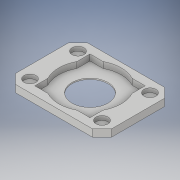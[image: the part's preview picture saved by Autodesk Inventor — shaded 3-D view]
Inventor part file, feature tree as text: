
AUTODESK INVENTOR PART (.ipt)
format: ipt  version: 2019 (Build 230136000, 136)  size: 176,128 bytes
history: native  units: mm
features: extrude x5, sketch x5, chamfer x4
ambient origin geometry x8: Origin, YZ Plane, XZ Plane, XY Plane, X Axis, Y Axis, Z Axis, Center Point
bodies: Solid1 (feature_tree)
feature tree (14):
  extrude  "Extrusion1"  Depth=40.0mm
  extrude  "Extrusion2"  Depth=3.0mm
  extrude  "Extrusion3"  Depth=2.5mm TaperAngle=0.0deg
  extrude  "Extrusion4"  Depth=3.5mm TaperAngle=0.0deg
  chamfer  "Chamfer1"  Distance=5.0mm
  chamfer  "Chamfer2"  Distance=5.0mm
  chamfer  "Chamfer3"  Distance=5.0mm
  chamfer  "Chamfer4"  Distance=15.0mm
  extrude  "Extrusion5"  Depth=2.5mm
  sketch  "Sketch1"  dims[d0=30.0mm d1=40.0mm]
  sketch  "Sketch2"  dims[d2=3.0mm d3=0.0mm d4=20.0mm]
  sketch  "Sketch3"  dims[d5=26.0mm d6=2.5mm d7=0.0mm]
  sketch  "Sketch4"  dims[d8=15.0mm d9=3.5mm d10=0.0mm]
  sketch  "Sketch5"  dims[d11=5.0mm d12=5.0mm d13=5.0mm d14=5.0mm d15=15.0mm d16=15.0mm d17=15.0mm d18=15.0mm d19=10.0mm d20=10.0mm d21=10.0mm d22=10.0mm d23=1.7mm d24=0.0mm d25=15.0mm d26=4.0mm d27=2.0mm d28=45.0deg d29=23.0mm d30=23.0mm d31=3.5mm d32=8.5mm d33=4.0mm d34=2.0mm d35=45.0deg d36=4.0mm d37=2.0mm d38=45.0deg d39=4.0mm d40=2.0mm d41=45.0deg d42=23.0mm d43=23.0mm d44=3.5mm d45=8.5mm d46=2.5mm d47=0.0mm]
